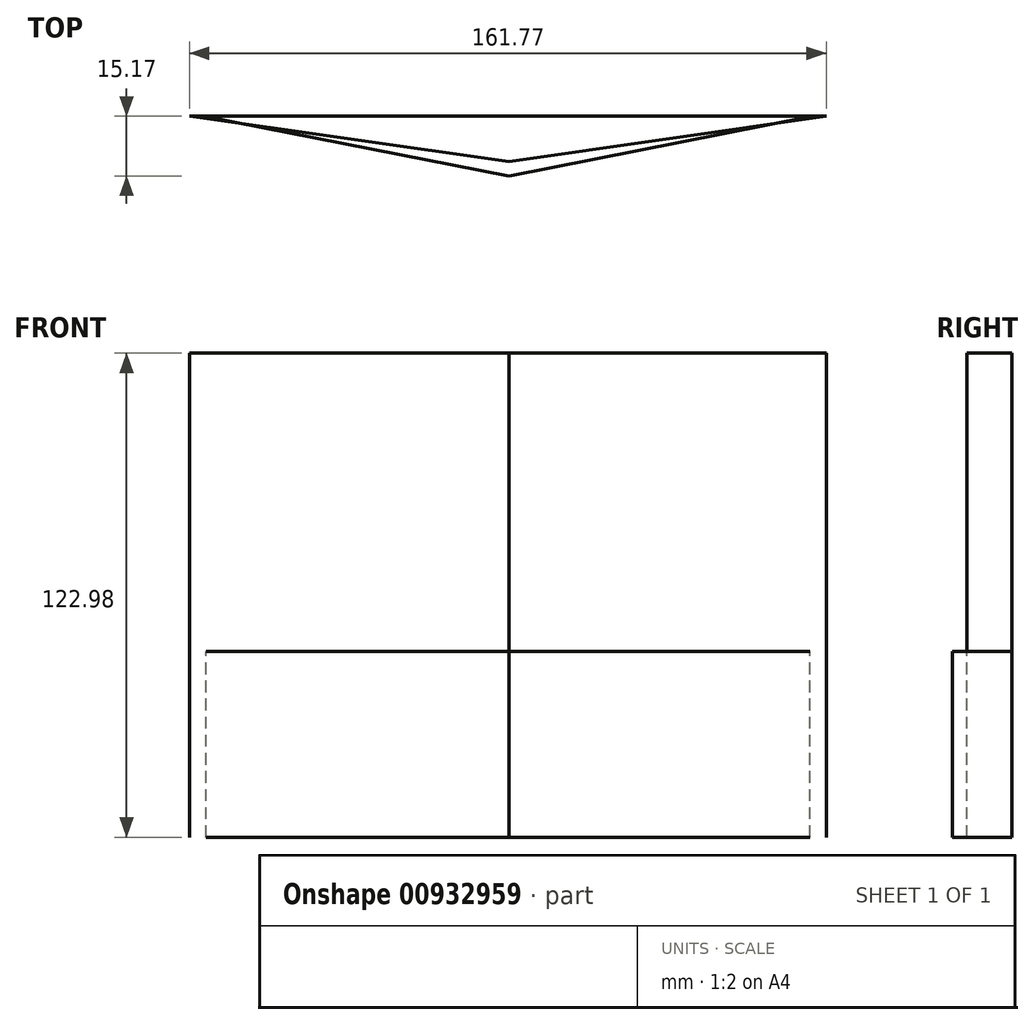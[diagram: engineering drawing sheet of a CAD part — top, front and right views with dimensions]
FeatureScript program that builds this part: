
annotation { "Feature Type Name" : "Feature", "Feature Type Description" : "" }
export const myFeature = defineFeature(function(context is Context, id is Id, definition is map)
    precondition{}
    {
        {
            var Q0;
            Q0=qCreatedBy(makeId("Top.planeOp"),FACE);
            var sketch = newSketch(context, id + "F0", { "sketchPlane" : qUnion([Q0])});
            skLineSegment(sketch, "E0", {"start": v(0, 0) * mm, "end": v(76.34, 15.14) * mm});
            skLineSegment(sketch, "E1", {"start": v(76.34, 15.14) * mm, "end": v(-76.97, 15.14) * mm});
            skLineSegment(sketch, "E2", {"start": v(0, 0) * mm, "end": v(-76.97, 15.14) * mm});
            skSolve(sketch);
        }
        {
            var Q0;
            Q0=sQuery(id+"F0.wireOp",EDGE,"E0");
            var Q1;
            Q1=sQuery(id+"F0.wireOp",EDGE,"E2");
            extrude(context, id + "F1", {"bodyType" : ToolBodyType.SURFACE, "surfaceEntities" : qUnion([Q0, Q1]), "depth" : 47.2 * mm, "offsetDistance" : 25.4 * mm});
        }
        {
            var Q0;
            Q0=qCreatedBy(makeId("Top.planeOp"),FACE);
            var sketch = newSketch(context, id + "F2", { "sketchPlane" : qUnion([Q0])});
            skLineSegment(sketch, "E3", {"start": v(-81.22, 15.17) * mm, "end": v(80.55, 15.17) * mm});
            skLineSegment(sketch, "E4", {"start": v(80.55, 15.17) * mm, "end": v(0, 3.68) * mm});
            skLineSegment(sketch, "E5", {"start": v(0, 3.68) * mm, "end": v(-81.22, 15.17) * mm});
            skLineSegment(sketch, "E6", {"start": v(0, 0) * mm, "end": v(0, 15.17) * mm});
            skSolve(sketch);
        }
        {
            var Q0;
            Q0=sQuery(id+"F2.wireOp",EDGE,"E4");
            var Q1;
            Q1=sQuery(id+"F2.wireOp",EDGE,"E5");
            var Q2;
            Q2=sQuery(id+"F2.wireOp",EDGE,"E3");
            extrude(context, id + "F3", {"bodyType" : ToolBodyType.SURFACE, "surfaceEntities" : qUnion([Q0, Q1, Q2]), "depth" : 122.98 * mm, "offsetDistance" : 25.4 * mm});
        }
    });
